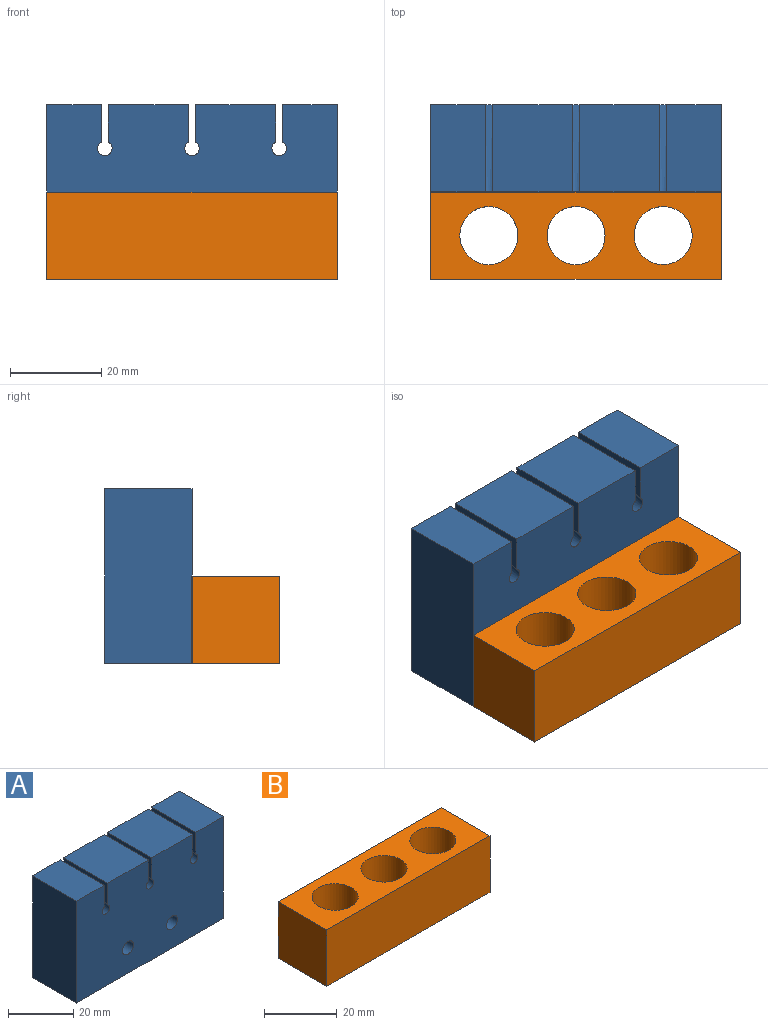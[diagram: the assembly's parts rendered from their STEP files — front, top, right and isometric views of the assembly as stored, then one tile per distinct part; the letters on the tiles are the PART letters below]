
ASSEMBLY  parts=2 mates=1
PART A: 22 faces, bbox 63.5x19.1x38.1 mm
  f0: plane 63.5x19.05mm, normal (0,0,-1), area 1209.7mm2, adj f1,f7,f9,f10
  f1: plane 38.1x19.05mm, normal (-1,0,0), area 725.8mm2, adj f0,f4,f7,f10
  f2: cylinder r=2.38mm len=16.67mm, axis (0,1,0), area 249.4mm2, adj f7,f17
  f3: cylinder r=2.38mm len=16.67mm, axis (0,1,0), area 249.4mm2, adj f7,f18
  f4: plane 19.05x11.91mm, normal (0,0,1), area 226.8mm2, adj f1,f7,f10,f12
  f5: plane 19.05x17.46mm, normal (0,0,1), area 332.7mm2, adj f7,f10,f14,f15
  f6: plane 19.05x11.91mm, normal (0,0,1), area 226.8mm2, adj f7,f9,f10,f16
  f7: plane 63.5x38.1mm, normal (0,-1,0), area 2321.8mm2, adj f0,f1,f2,f3,f4,f5,f6,f8
  f8: plane 19.05x17.46mm, normal (0,0,1), area 332.7mm2, adj f7,f10,f11,f13
  f9: plane 38.1x19.05mm, normal (1,0,0), area 725.8mm2, adj f0,f6,f7,f10
  f10: plane 63.5x38.1mm, normal (0,1,0), area 1841.2mm2, adj f0,f1,f4,f5,f6,f8,f9,f11
  f11: plane 19.05x8.15mm, normal (-1,0,0), area 104.3mm2, adj f7,f8,f10,f21
  f12: plane 19.05x8.15mm, normal (1,0,0), area 104.3mm2, adj f4,f7,f10,f21
  f13: plane 19.05x8.15mm, normal (1,0,0), area 104.3mm2, adj f7,f8,f10,f20
  f14: plane 19.05x8.15mm, normal (-1,0,0), area 104.3mm2, adj f5,f7,f10,f20
  f15: plane 19.05x8.15mm, normal (1,0,0), area 104.3mm2, adj f5,f7,f10,f19
  f16: plane 19.05x8.15mm, normal (-1,0,0), area 104.3mm2, adj f6,f7,f10,f19
  f17: cone r=2.38mm half-angle=45deg, axis (0,1,0), area 75.6mm2, adj f2,f10
  f18: cone r=2.38mm half-angle=45deg, axis (0,1,0), area 75.6mm2, adj f3,f10
  f19: cone r=6.69mm half-angle=15deg, axis (0,1,0), area 481.3mm2, adj f7,f10,f15,f16
  f20: cone r=6.69mm half-angle=15deg, axis (0,1,0), area 481.3mm2, adj f7,f10,f13,f14
  f21: cone r=6.69mm half-angle=15deg, axis (0,1,0), area 481.3mm2, adj f7,f10,f11,f12
PART B: 13 faces, bbox 63.5x19.1x19.1 mm
  f0: cone r=0mm half-angle=59deg, axis (0,1,0), area 20.8mm2, adj f1
  f1: cylinder r=2.38mm len=6.35mm, axis (0,1,0), area 95mm2, adj f0,f2
  f2: plane 63.5x19.05mm, normal (0,1,0), area 1174mm2, adj f1,f4,f5,f6,f7,f9
  f3: cone r=0mm half-angle=59deg, axis (0,1,0), area 20.8mm2, adj f4
  f4: cylinder r=2.38mm len=6.35mm, axis (0,1,0), area 95mm2, adj f2,f3
  f5: plane 19.05x19.05mm, normal (-1,0,0), area 362.9mm2, adj f2,f6,f8,f9
  f6: plane 63.5x19.05mm, normal (0,0,-1), area 829.6mm2, adj f2,f5,f7,f8,f10,f11,f12
  f7: plane 19.05x19.05mm, normal (1,0,0), area 362.9mm2, adj f2,f6,f8,f9
  f8: plane 63.5x19.05mm, normal (0,-1,0), area 1209.7mm2, adj f5,f6,f7,f9
  f9: plane 63.5x19.05mm, normal (0,0,1), area 829.6mm2, adj f2,f5,f7,f8,f10,f11,f12
  f10: cylinder r=6.35mm len=19.05mm, axis (0,0,1), area 760.1mm2, adj f6,f9
  f11: cylinder r=6.35mm len=19.05mm, axis (0,0,1), area 760.1mm2, adj f6,f9
  f12: cylinder r=6.35mm len=19.05mm, axis (0,0,1), area 760.1mm2, adj f6,f9
PLACE A t=(-21.87,19.06,-9.73)mm
PLACE B t=(-21.87,6.36,-9.73)mm
MATE fastened B.f2 <-> A.f7  axis (0,1,0) through (9.88,0.01,-9.73)mm
